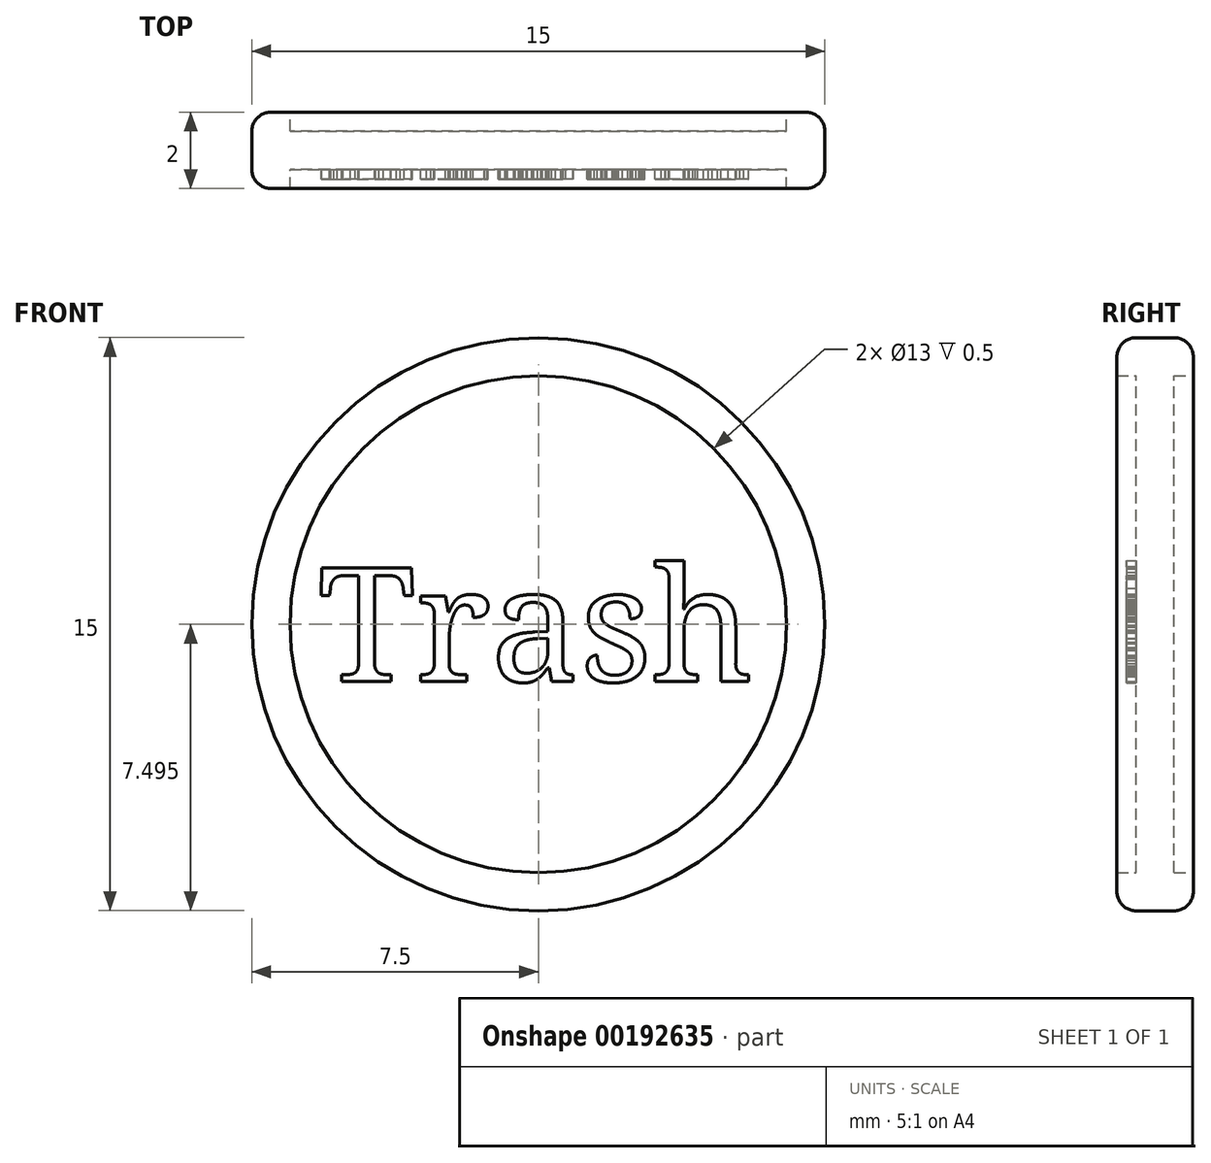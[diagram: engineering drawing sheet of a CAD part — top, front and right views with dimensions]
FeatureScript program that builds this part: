
annotation { "Feature Type Name" : "Feature", "Feature Type Description" : "" }
export const myFeature = defineFeature(function(context is Context, id is Id, definition is map)
    precondition{}
    {
        {
            var Q0;
            Q0=qCreatedBy(makeId("Front.planeOp"),FACE);
            var sketch = newSketch(context, id + "F0", { "sketchPlane" : qUnion([Q0])});
            skCircle(sketch, "E0", {"center": v(-67.05, 36.37) * mm, "radius": 7.5 * mm});
            skCircle(sketch, "E1", {"center": v(-67.05, 36.37) * mm, "radius": 6.5 * mm});
            skText(sketch, "E2", { "text": "Trash", "fontName": "NotoSerif-Regular.ttf"});
            const initialGuessF0  = {"E2": [-0.07282, 0.03487, 1, 0, 0.003]};
            skSetInitialGuess(sketch, initialGuessF0);
            skSolve(sketch);
        }
        {
            var Q0;
            Q0=makeQuery(id+"F0.imprint","IMPRINT",FACE,{"disambiguationData":[TD([[makeQuery(id+"F0.imprint","IMPRINT",EDGE,{"derivedFrom":sQuery(id+"F0.wireOp",EDGE,"E1")}),1.0]])]});
            var Q1;
            Q1=makeQuery(id+"F0.imprint","IMPRINT",FACE,{"disambiguationData":[TD([[makeQuery(id+"F0.imprint","IMPRINT",EDGE,{"derivedFrom":sQuery(id+"F0.wireOp",EDGE,"E2.sketch_text.stroke-74")}),1.0]])]});
            extrude(context, id + "F1", {"entities" : qUnion([Q0, Q1]), "endBound" : BoundingType.SYMMETRIC, "depth" : 1 * mm});
        }
        {
            var Q0;
            Q0=makeQuery(id+"F0.imprint","IMPRINT",FACE,{"disambiguationData":[TD([[makeQuery(id+"F0.imprint","IMPRINT",EDGE,{"derivedFrom":sQuery(id+"F0.wireOp",EDGE,"E0")}),1.0]])]});
            extrude(context, id + "F2", {"entities" : qUnion([Q0]), "operationType" : NewBodyOperationType.ADD, "endBound" : BoundingType.SYMMETRIC, "depth" : 2 * mm});
        }
        {
            var Q0;
            Q0=makeQuery(id+"F0.imprint","IMPRINT",FACE,{"disambiguationData":[TD([[makeQuery(id+"F0.imprint","IMPRINT",EDGE,{"derivedFrom":sQuery(id+"F0.wireOp",EDGE,"E2.sketch_text.stroke-0")}),-1.0]])]});
            var Q1;
            Q1=makeQuery(id+"F0.imprint","IMPRINT",FACE,{"disambiguationData":[TD([[makeQuery(id+"F0.imprint","IMPRINT",EDGE,{"derivedFrom":sQuery(id+"F0.wireOp",EDGE,"E2.sketch_text.stroke-32")}),-1.0]])]});
            var Q2;
            Q2=makeQuery(id+"F0.imprint","IMPRINT",FACE,{"disambiguationData":[TD([[makeQuery(id+"F0.imprint","IMPRINT",EDGE,{"derivedFrom":sQuery(id+"F0.wireOp",EDGE,"E2.sketch_text.stroke-74")}),-1.0]])]});
            var Q3;
            Q3=makeQuery(id+"F0.imprint","IMPRINT",FACE,{"disambiguationData":[TD([[makeQuery(id+"F0.imprint","IMPRINT",EDGE,{"derivedFrom":sQuery(id+"F0.wireOp",EDGE,"E2.sketch_text.stroke-126")}),-1.0]])]});
            var Q4;
            Q4=makeQuery(id+"F0.imprint","IMPRINT",FACE,{"disambiguationData":[TD([[makeQuery(id+"F0.imprint","IMPRINT",EDGE,{"derivedFrom":sQuery(id+"F0.wireOp",EDGE,"E2.sketch_text.stroke-178")}),-1.0]])]});
            extrude(context, id + "F3", {"entities" : qUnion([Q0, Q1, Q2, Q3, Q4]), "operationType" : NewBodyOperationType.ADD, "depth" : 1.5 / 2 * mm});
        }
        {
            var Q0;
            Q0=makeQuery(id+"F2.opExtrude","CAP_EDGE",EDGE,{"disambiguationData":[OSD([sQuery(id+"F0.wireOp",EDGE,"E0")])],"isStart":false});
            var Q1;
            Q1=makeQuery(id+"F2.opExtrude","CAP_EDGE",EDGE,{"disambiguationData":[OSD([sQuery(id+"F0.wireOp",EDGE,"E0")])],"isStart":true});
            fillet(context, id + "F4", {"entities" : qUnion([Q0, Q1]), "radius" : 0.5 * mm, "tangentPropagation" : true, "allowEdgeOverflow" : false});
        }
        {
            var Q0;
            Q0=makeQuery(id+"F3.opExtrude","CAP_FACE",FACE,{"disambiguationData":[OSD([sQuery(id+"F0.wireOp",EDGE,"E2.sketch_text.stroke-178"),sQuery(id+"F0.wireOp",EDGE,"E2.sketch_text.stroke-179"),sQuery(id+"F0.wireOp",EDGE,"E2.sketch_text.stroke-180"),sQuery(id+"F0.wireOp",EDGE,"E2.sketch_text.stroke-181"),sQuery(id+"F0.wireOp",EDGE,"E2.sketch_text.stroke-182"),sQuery(id+"F0.wireOp",EDGE,"E2.sketch_text.stroke-183"),sQuery(id+"F0.wireOp",EDGE,"E2.sketch_text.stroke-184"),sQuery(id+"F0.wireOp",EDGE,"E2.sketch_text.stroke-185"),sQuery(id+"F0.wireOp",EDGE,"E2.sketch_text.stroke-186"),sQuery(id+"F0.wireOp",EDGE,"E2.sketch_text.stroke-187"),sQuery(id+"F0.wireOp",EDGE,"E2.sketch_text.stroke-188"),sQuery(id+"F0.wireOp",EDGE,"E2.sketch_text.stroke-189"),sQuery(id+"F0.wireOp",EDGE,"E2.sketch_text.stroke-190"),sQuery(id+"F0.wireOp",EDGE,"E2.sketch_text.stroke-191"),sQuery(id+"F0.wireOp",EDGE,"E2.sketch_text.stroke-192"),sQuery(id+"F0.wireOp",EDGE,"E2.sketch_text.stroke-193"),sQuery(id+"F0.wireOp",EDGE,"E2.sketch_text.stroke-194"),sQuery(id+"F0.wireOp",EDGE,"E2.sketch_text.stroke-195"),sQuery(id+"F0.wireOp",EDGE,"E2.sketch_text.stroke-196"),sQuery(id+"F0.wireOp",EDGE,"E2.sketch_text.stroke-197"),sQuery(id+"F0.wireOp",EDGE,"E2.sketch_text.stroke-198"),sQuery(id+"F0.wireOp",EDGE,"E2.sketch_text.stroke-199"),sQuery(id+"F0.wireOp",EDGE,"E2.sketch_text.stroke-200"),sQuery(id+"F0.wireOp",EDGE,"E2.sketch_text.stroke-201"),sQuery(id+"F0.wireOp",EDGE,"E2.sketch_text.stroke-202"),sQuery(id+"F0.wireOp",EDGE,"E2.sketch_text.stroke-203"),sQuery(id+"F0.wireOp",EDGE,"E2.sketch_text.stroke-204"),sQuery(id+"F0.wireOp",EDGE,"E2.sketch_text.stroke-205"),sQuery(id+"F0.wireOp",EDGE,"E2.sketch_text.stroke-206"),sQuery(id+"F0.wireOp",EDGE,"E2.sketch_text.stroke-207"),sQuery(id+"F0.wireOp",EDGE,"E2.sketch_text.stroke-208"),sQuery(id+"F0.wireOp",EDGE,"E2.sketch_text.stroke-209"),sQuery(id+"F0.wireOp",EDGE,"E2.sketch_text.stroke-210"),sQuery(id+"F0.wireOp",EDGE,"E2.sketch_text.stroke-211"),sQuery(id+"F0.wireOp",EDGE,"E2.sketch_text.stroke-212"),sQuery(id+"F0.wireOp",EDGE,"E2.sketch_text.stroke-213"),sQuery(id+"F0.wireOp",EDGE,"E2.sketch_text.stroke-214"),sQuery(id+"F0.wireOp",EDGE,"E2.sketch_text.stroke-215"),sQuery(id+"F0.wireOp",EDGE,"E2.sketch_text.stroke-216"),sQuery(id+"F0.wireOp",EDGE,"E2.sketch_text.stroke-217"),sQuery(id+"F0.wireOp",EDGE,"E2.sketch_text.stroke-218"),sQuery(id+"F0.wireOp",EDGE,"E2.sketch_text.stroke-219"),sQuery(id+"F0.wireOp",EDGE,"E2.sketch_text.stroke-220"),sQuery(id+"F0.wireOp",EDGE,"E2.sketch_text.stroke-221"),sQuery(id+"F0.wireOp",EDGE,"E2.sketch_text.stroke-222"),sQuery(id+"F0.wireOp",EDGE,"E2.sketch_text.stroke-223"),sQuery(id+"F0.wireOp",EDGE,"E2.sketch_text.stroke-224"),sQuery(id+"F0.wireOp",EDGE,"E2.sketch_text.stroke-225"),sQuery(id+"F0.wireOp",EDGE,"E2.sketch_text.stroke-226")])],"isStart":true});
            var Q1;
            Q1=makeQuery(id+"F3.opExtrude","CAP_FACE",FACE,{"disambiguationData":[OSD([sQuery(id+"F0.wireOp",EDGE,"E2.sketch_text.stroke-126"),sQuery(id+"F0.wireOp",EDGE,"E2.sketch_text.stroke-127"),sQuery(id+"F0.wireOp",EDGE,"E2.sketch_text.stroke-128"),sQuery(id+"F0.wireOp",EDGE,"E2.sketch_text.stroke-129"),sQuery(id+"F0.wireOp",EDGE,"E2.sketch_text.stroke-130"),sQuery(id+"F0.wireOp",EDGE,"E2.sketch_text.stroke-131"),sQuery(id+"F0.wireOp",EDGE,"E2.sketch_text.stroke-132"),sQuery(id+"F0.wireOp",EDGE,"E2.sketch_text.stroke-133"),sQuery(id+"F0.wireOp",EDGE,"E2.sketch_text.stroke-134"),sQuery(id+"F0.wireOp",EDGE,"E2.sketch_text.stroke-135"),sQuery(id+"F0.wireOp",EDGE,"E2.sketch_text.stroke-136"),sQuery(id+"F0.wireOp",EDGE,"E2.sketch_text.stroke-137"),sQuery(id+"F0.wireOp",EDGE,"E2.sketch_text.stroke-138"),sQuery(id+"F0.wireOp",EDGE,"E2.sketch_text.stroke-139"),sQuery(id+"F0.wireOp",EDGE,"E2.sketch_text.stroke-140"),sQuery(id+"F0.wireOp",EDGE,"E2.sketch_text.stroke-141"),sQuery(id+"F0.wireOp",EDGE,"E2.sketch_text.stroke-142"),sQuery(id+"F0.wireOp",EDGE,"E2.sketch_text.stroke-143"),sQuery(id+"F0.wireOp",EDGE,"E2.sketch_text.stroke-144"),sQuery(id+"F0.wireOp",EDGE,"E2.sketch_text.stroke-145"),sQuery(id+"F0.wireOp",EDGE,"E2.sketch_text.stroke-146"),sQuery(id+"F0.wireOp",EDGE,"E2.sketch_text.stroke-147"),sQuery(id+"F0.wireOp",EDGE,"E2.sketch_text.stroke-148"),sQuery(id+"F0.wireOp",EDGE,"E2.sketch_text.stroke-149"),sQuery(id+"F0.wireOp",EDGE,"E2.sketch_text.stroke-150"),sQuery(id+"F0.wireOp",EDGE,"E2.sketch_text.stroke-151"),sQuery(id+"F0.wireOp",EDGE,"E2.sketch_text.stroke-152"),sQuery(id+"F0.wireOp",EDGE,"E2.sketch_text.stroke-153"),sQuery(id+"F0.wireOp",EDGE,"E2.sketch_text.stroke-154"),sQuery(id+"F0.wireOp",EDGE,"E2.sketch_text.stroke-155"),sQuery(id+"F0.wireOp",EDGE,"E2.sketch_text.stroke-156"),sQuery(id+"F0.wireOp",EDGE,"E2.sketch_text.stroke-157"),sQuery(id+"F0.wireOp",EDGE,"E2.sketch_text.stroke-158"),sQuery(id+"F0.wireOp",EDGE,"E2.sketch_text.stroke-159"),sQuery(id+"F0.wireOp",EDGE,"E2.sketch_text.stroke-160"),sQuery(id+"F0.wireOp",EDGE,"E2.sketch_text.stroke-161"),sQuery(id+"F0.wireOp",EDGE,"E2.sketch_text.stroke-162"),sQuery(id+"F0.wireOp",EDGE,"E2.sketch_text.stroke-163"),sQuery(id+"F0.wireOp",EDGE,"E2.sketch_text.stroke-164"),sQuery(id+"F0.wireOp",EDGE,"E2.sketch_text.stroke-165"),sQuery(id+"F0.wireOp",EDGE,"E2.sketch_text.stroke-166"),sQuery(id+"F0.wireOp",EDGE,"E2.sketch_text.stroke-167"),sQuery(id+"F0.wireOp",EDGE,"E2.sketch_text.stroke-168"),sQuery(id+"F0.wireOp",EDGE,"E2.sketch_text.stroke-169"),sQuery(id+"F0.wireOp",EDGE,"E2.sketch_text.stroke-170"),sQuery(id+"F0.wireOp",EDGE,"E2.sketch_text.stroke-171"),sQuery(id+"F0.wireOp",EDGE,"E2.sketch_text.stroke-172"),sQuery(id+"F0.wireOp",EDGE,"E2.sketch_text.stroke-173"),sQuery(id+"F0.wireOp",EDGE,"E2.sketch_text.stroke-174"),sQuery(id+"F0.wireOp",EDGE,"E2.sketch_text.stroke-175"),sQuery(id+"F0.wireOp",EDGE,"E2.sketch_text.stroke-176"),sQuery(id+"F0.wireOp",EDGE,"E2.sketch_text.stroke-177")])],"isStart":true});
            var Q2;
            Q2=makeQuery(id+"F3.opExtrude","CAP_FACE",FACE,{"disambiguationData":[OSD([sQuery(id+"F0.wireOp",EDGE,"E2.sketch_text.stroke-74"),sQuery(id+"F0.wireOp",EDGE,"E2.sketch_text.stroke-75"),sQuery(id+"F0.wireOp",EDGE,"E2.sketch_text.stroke-76"),sQuery(id+"F0.wireOp",EDGE,"E2.sketch_text.stroke-77"),sQuery(id+"F0.wireOp",EDGE,"E2.sketch_text.stroke-78"),sQuery(id+"F0.wireOp",EDGE,"E2.sketch_text.stroke-79"),sQuery(id+"F0.wireOp",EDGE,"E2.sketch_text.stroke-80"),sQuery(id+"F0.wireOp",EDGE,"E2.sketch_text.stroke-81"),sQuery(id+"F0.wireOp",EDGE,"E2.sketch_text.stroke-82"),sQuery(id+"F0.wireOp",EDGE,"E2.sketch_text.stroke-83"),sQuery(id+"F0.wireOp",EDGE,"E2.sketch_text.stroke-84"),sQuery(id+"F0.wireOp",EDGE,"E2.sketch_text.stroke-85"),sQuery(id+"F0.wireOp",EDGE,"E2.sketch_text.stroke-86"),sQuery(id+"F0.wireOp",EDGE,"E2.sketch_text.stroke-87"),sQuery(id+"F0.wireOp",EDGE,"E2.sketch_text.stroke-88"),sQuery(id+"F0.wireOp",EDGE,"E2.sketch_text.stroke-89"),sQuery(id+"F0.wireOp",EDGE,"E2.sketch_text.stroke-90"),sQuery(id+"F0.wireOp",EDGE,"E2.sketch_text.stroke-91"),sQuery(id+"F0.wireOp",EDGE,"E2.sketch_text.stroke-92"),sQuery(id+"F0.wireOp",EDGE,"E2.sketch_text.stroke-93"),sQuery(id+"F0.wireOp",EDGE,"E2.sketch_text.stroke-94"),sQuery(id+"F0.wireOp",EDGE,"E2.sketch_text.stroke-95"),sQuery(id+"F0.wireOp",EDGE,"E2.sketch_text.stroke-96"),sQuery(id+"F0.wireOp",EDGE,"E2.sketch_text.stroke-97"),sQuery(id+"F0.wireOp",EDGE,"E2.sketch_text.stroke-98"),sQuery(id+"F0.wireOp",EDGE,"E2.sketch_text.stroke-99"),sQuery(id+"F0.wireOp",EDGE,"E2.sketch_text.stroke-100"),sQuery(id+"F0.wireOp",EDGE,"E2.sketch_text.stroke-101"),sQuery(id+"F0.wireOp",EDGE,"E2.sketch_text.stroke-102"),sQuery(id+"F0.wireOp",EDGE,"E2.sketch_text.stroke-103"),sQuery(id+"F0.wireOp",EDGE,"E2.sketch_text.stroke-104"),sQuery(id+"F0.wireOp",EDGE,"E2.sketch_text.stroke-105"),sQuery(id+"F0.wireOp",EDGE,"E2.sketch_text.stroke-106"),sQuery(id+"F0.wireOp",EDGE,"E2.sketch_text.stroke-107"),sQuery(id+"F0.wireOp",EDGE,"E2.sketch_text.stroke-108"),sQuery(id+"F0.wireOp",EDGE,"E2.sketch_text.stroke-109"),sQuery(id+"F0.wireOp",EDGE,"E2.sketch_text.stroke-110"),sQuery(id+"F0.wireOp",EDGE,"E2.sketch_text.stroke-111"),sQuery(id+"F0.wireOp",EDGE,"E2.sketch_text.stroke-112"),sQuery(id+"F0.wireOp",EDGE,"E2.sketch_text.stroke-113"),sQuery(id+"F0.wireOp",EDGE,"E2.sketch_text.stroke-114"),sQuery(id+"F0.wireOp",EDGE,"E2.sketch_text.stroke-115"),sQuery(id+"F0.wireOp",EDGE,"E2.sketch_text.stroke-116"),sQuery(id+"F0.wireOp",EDGE,"E2.sketch_text.stroke-117"),sQuery(id+"F0.wireOp",EDGE,"E2.sketch_text.stroke-118"),sQuery(id+"F0.wireOp",EDGE,"E2.sketch_text.stroke-119"),sQuery(id+"F0.wireOp",EDGE,"E2.sketch_text.stroke-120"),sQuery(id+"F0.wireOp",EDGE,"E2.sketch_text.stroke-121"),sQuery(id+"F0.wireOp",EDGE,"E2.sketch_text.stroke-122"),sQuery(id+"F0.wireOp",EDGE,"E2.sketch_text.stroke-123"),sQuery(id+"F0.wireOp",EDGE,"E2.sketch_text.stroke-124"),sQuery(id+"F0.wireOp",EDGE,"E2.sketch_text.stroke-125")])],"isStart":true});
            var Q3;
            Q3=makeQuery(id+"F3.opExtrude","CAP_FACE",FACE,{"disambiguationData":[OSD([sQuery(id+"F0.wireOp",EDGE,"E2.sketch_text.stroke-32"),sQuery(id+"F0.wireOp",EDGE,"E2.sketch_text.stroke-33"),sQuery(id+"F0.wireOp",EDGE,"E2.sketch_text.stroke-34"),sQuery(id+"F0.wireOp",EDGE,"E2.sketch_text.stroke-35"),sQuery(id+"F0.wireOp",EDGE,"E2.sketch_text.stroke-36"),sQuery(id+"F0.wireOp",EDGE,"E2.sketch_text.stroke-37"),sQuery(id+"F0.wireOp",EDGE,"E2.sketch_text.stroke-38"),sQuery(id+"F0.wireOp",EDGE,"E2.sketch_text.stroke-39"),sQuery(id+"F0.wireOp",EDGE,"E2.sketch_text.stroke-40"),sQuery(id+"F0.wireOp",EDGE,"E2.sketch_text.stroke-41"),sQuery(id+"F0.wireOp",EDGE,"E2.sketch_text.stroke-42"),sQuery(id+"F0.wireOp",EDGE,"E2.sketch_text.stroke-43"),sQuery(id+"F0.wireOp",EDGE,"E2.sketch_text.stroke-44"),sQuery(id+"F0.wireOp",EDGE,"E2.sketch_text.stroke-45"),sQuery(id+"F0.wireOp",EDGE,"E2.sketch_text.stroke-46"),sQuery(id+"F0.wireOp",EDGE,"E2.sketch_text.stroke-47"),sQuery(id+"F0.wireOp",EDGE,"E2.sketch_text.stroke-48"),sQuery(id+"F0.wireOp",EDGE,"E2.sketch_text.stroke-49"),sQuery(id+"F0.wireOp",EDGE,"E2.sketch_text.stroke-50"),sQuery(id+"F0.wireOp",EDGE,"E2.sketch_text.stroke-51"),sQuery(id+"F0.wireOp",EDGE,"E2.sketch_text.stroke-52"),sQuery(id+"F0.wireOp",EDGE,"E2.sketch_text.stroke-53"),sQuery(id+"F0.wireOp",EDGE,"E2.sketch_text.stroke-54"),sQuery(id+"F0.wireOp",EDGE,"E2.sketch_text.stroke-55"),sQuery(id+"F0.wireOp",EDGE,"E2.sketch_text.stroke-56"),sQuery(id+"F0.wireOp",EDGE,"E2.sketch_text.stroke-57"),sQuery(id+"F0.wireOp",EDGE,"E2.sketch_text.stroke-58"),sQuery(id+"F0.wireOp",EDGE,"E2.sketch_text.stroke-59"),sQuery(id+"F0.wireOp",EDGE,"E2.sketch_text.stroke-60"),sQuery(id+"F0.wireOp",EDGE,"E2.sketch_text.stroke-61"),sQuery(id+"F0.wireOp",EDGE,"E2.sketch_text.stroke-62"),sQuery(id+"F0.wireOp",EDGE,"E2.sketch_text.stroke-63"),sQuery(id+"F0.wireOp",EDGE,"E2.sketch_text.stroke-64"),sQuery(id+"F0.wireOp",EDGE,"E2.sketch_text.stroke-65"),sQuery(id+"F0.wireOp",EDGE,"E2.sketch_text.stroke-66"),sQuery(id+"F0.wireOp",EDGE,"E2.sketch_text.stroke-67"),sQuery(id+"F0.wireOp",EDGE,"E2.sketch_text.stroke-68"),sQuery(id+"F0.wireOp",EDGE,"E2.sketch_text.stroke-69"),sQuery(id+"F0.wireOp",EDGE,"E2.sketch_text.stroke-70"),sQuery(id+"F0.wireOp",EDGE,"E2.sketch_text.stroke-71"),sQuery(id+"F0.wireOp",EDGE,"E2.sketch_text.stroke-72"),sQuery(id+"F0.wireOp",EDGE,"E2.sketch_text.stroke-73")])],"isStart":true});
            var Q4;
            Q4=makeQuery(id+"F3.opExtrude","CAP_FACE",FACE,{"disambiguationData":[OSD([sQuery(id+"F0.wireOp",EDGE,"E2.sketch_text.stroke-0"),sQuery(id+"F0.wireOp",EDGE,"E2.sketch_text.stroke-1"),sQuery(id+"F0.wireOp",EDGE,"E2.sketch_text.stroke-2"),sQuery(id+"F0.wireOp",EDGE,"E2.sketch_text.stroke-3"),sQuery(id+"F0.wireOp",EDGE,"E2.sketch_text.stroke-4"),sQuery(id+"F0.wireOp",EDGE,"E2.sketch_text.stroke-5"),sQuery(id+"F0.wireOp",EDGE,"E2.sketch_text.stroke-6"),sQuery(id+"F0.wireOp",EDGE,"E2.sketch_text.stroke-7"),sQuery(id+"F0.wireOp",EDGE,"E2.sketch_text.stroke-8"),sQuery(id+"F0.wireOp",EDGE,"E2.sketch_text.stroke-9"),sQuery(id+"F0.wireOp",EDGE,"E2.sketch_text.stroke-10"),sQuery(id+"F0.wireOp",EDGE,"E2.sketch_text.stroke-11"),sQuery(id+"F0.wireOp",EDGE,"E2.sketch_text.stroke-12"),sQuery(id+"F0.wireOp",EDGE,"E2.sketch_text.stroke-13"),sQuery(id+"F0.wireOp",EDGE,"E2.sketch_text.stroke-14"),sQuery(id+"F0.wireOp",EDGE,"E2.sketch_text.stroke-15"),sQuery(id+"F0.wireOp",EDGE,"E2.sketch_text.stroke-16"),sQuery(id+"F0.wireOp",EDGE,"E2.sketch_text.stroke-17"),sQuery(id+"F0.wireOp",EDGE,"E2.sketch_text.stroke-18"),sQuery(id+"F0.wireOp",EDGE,"E2.sketch_text.stroke-19"),sQuery(id+"F0.wireOp",EDGE,"E2.sketch_text.stroke-20"),sQuery(id+"F0.wireOp",EDGE,"E2.sketch_text.stroke-21"),sQuery(id+"F0.wireOp",EDGE,"E2.sketch_text.stroke-22"),sQuery(id+"F0.wireOp",EDGE,"E2.sketch_text.stroke-23"),sQuery(id+"F0.wireOp",EDGE,"E2.sketch_text.stroke-24"),sQuery(id+"F0.wireOp",EDGE,"E2.sketch_text.stroke-25"),sQuery(id+"F0.wireOp",EDGE,"E2.sketch_text.stroke-26"),sQuery(id+"F0.wireOp",EDGE,"E2.sketch_text.stroke-27"),sQuery(id+"F0.wireOp",EDGE,"E2.sketch_text.stroke-28"),sQuery(id+"F0.wireOp",EDGE,"E2.sketch_text.stroke-29"),sQuery(id+"F0.wireOp",EDGE,"E2.sketch_text.stroke-30"),sQuery(id+"F0.wireOp",EDGE,"E2.sketch_text.stroke-31")])],"isStart":true});
            extrude(context, id + "F5", {"entities" : qUnion([Q0, Q1, Q2, Q3, Q4]), "operationType" : NewBodyOperationType.ADD, "depth" : 1 / 2 * mm});
        }
    });
